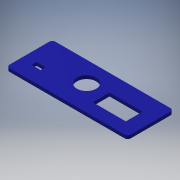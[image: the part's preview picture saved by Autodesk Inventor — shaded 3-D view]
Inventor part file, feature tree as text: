
AUTODESK INVENTOR PART (.ipt)
format: ipt  version: 2016 (Build 200138000, 138)  size: 199,168 bytes
history: native  units: mm
features: sketch x4, extrude x3, other x2, fillet x1
ambient origin geometry x8: Origin, YZ Plane, XZ Plane, XY Plane, X Axis, Y Axis, Z Axis, Center Point
bodies: Solid1 (feature_tree)
feature tree (10):
  extrude  "Extrusion1"  Depth=22.5mm
  fillet  "Fillet1"  Radius=1.6mm
  extrude  "Extrusion2"  Depth=1.5mm
  extrude  "Extrusion4"  Depth=10.0mm
  other  "Decal1"
  sketch  "Sketch1"  dims[d0=59.5mm d1=22.5mm d2=1.6mm d3=0.0mm]
  sketch  "Sketch2"  dims[d4=1.5mm d5=9.5mm]
  sketch  "Sketch4"  dims[d6=10.0mm d7=0.0mm d15=12.51mm]
  sketch  "Sketch5"  dims[d16=26.801mm d17=6.01mm d18=1.401mm d19=4.4mm d20=2.4mm d21=6.35mm d22=2.0mm d23=6.01mm d24=1.401mm d25=16.2mm d26=8.2mm d28=43.18mm d29=0.1mm d30=10.0mm d31=0.0mm]
  other  "Image1"
